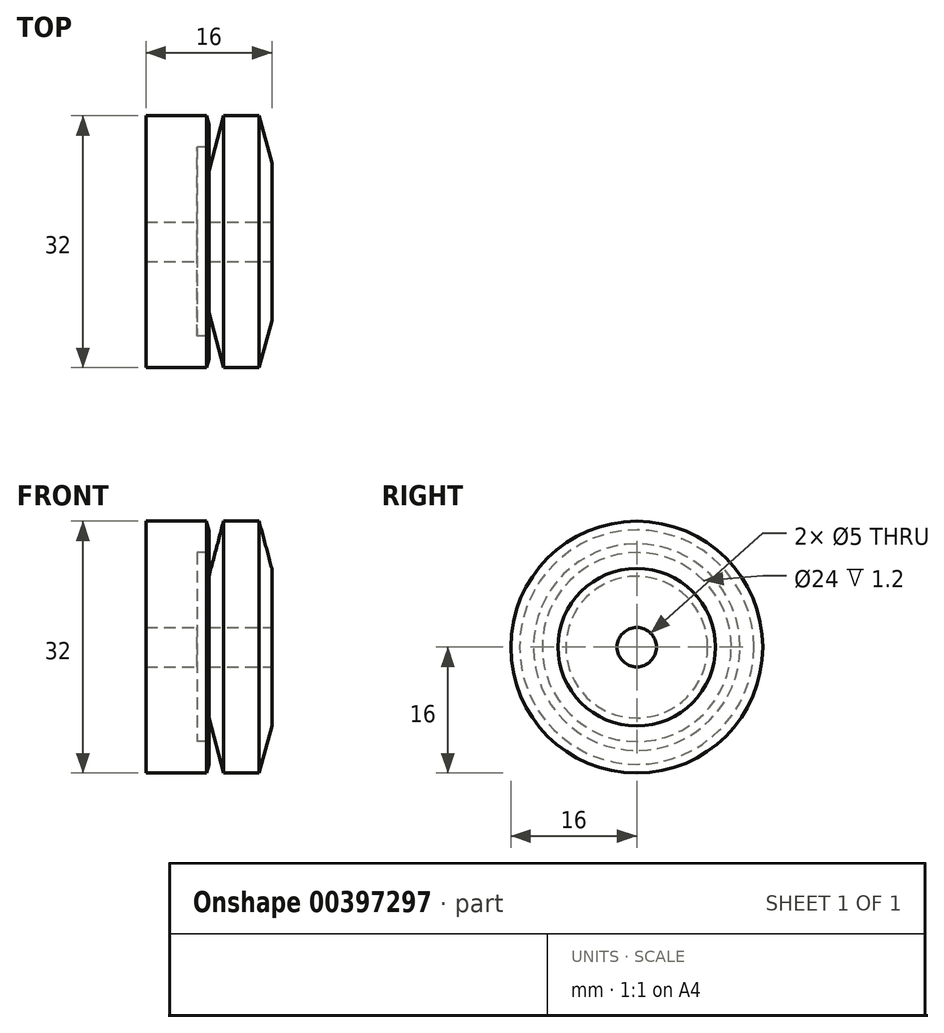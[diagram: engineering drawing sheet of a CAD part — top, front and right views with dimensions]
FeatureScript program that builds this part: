
annotation { "Feature Type Name" : "Feature", "Feature Type Description" : "" }
export const myFeature = defineFeature(function(context is Context, id is Id, definition is map)
    precondition{}
    {
        {
            var Q0;
            Q0=qCreatedBy(makeId("Front.planeOp"),FACE);
            var sketch = newSketch(context, id + "F0", { "sketchPlane" : qUnion([Q0])});
            skLineSegment(sketch, "E0", {"start": v(0, 3) * mm, "end": v(0, 16) * mm});
            skLineSegment(sketch, "E1", {"start": v(0, 16) * mm, "end": v(8, 16) * mm});
            skLineSegment(sketch, "E2", {"start": v(8, 16) * mm, "end": v(8, 12) * mm});
            skLineSegment(sketch, "E3", {"start": v(8, 6) * mm, "end": v(6.5, 6) * mm});
            skLineSegment(sketch, "E4", {"start": v(6.5, 6) * mm, "end": v(6.5, 12) * mm});
            skLineSegment(sketch, "E5", {"start": v(6.5, 12) * mm, "end": v(8, 12) * mm});
            skPoint(sketch, "E6.orphan", {"position": v(0, 0) * mm});
            skLineSegment(sketch, "E7", {"start": v(8, 0) * mm, "end": v(16, 0) * mm});
            skLineSegment(sketch, "E8", {"start": v(16, 0) * mm, "end": v(16, 16) * mm});
            skLineSegment(sketch, "E9", {"start": v(16, 16) * mm, "end": v(9.88, 16) * mm});
            skLineSegment(sketch, "E10", {"start": v(9.88, 16) * mm, "end": v(8, 9) * mm});
            skLineSegment(sketch, "E11", {"start": v(0, 0) * mm, "end": v(0, 16) * mm});
            skLineSegment(sketch, "E12", {"start": v(0, 3) * mm, "end": v(16, 3) * mm, "construction": true});
            skLineSegment(sketch, "E13", {"start": v(0, 0) * mm, "end": v(8, 0) * mm});
            skLineSegment(sketch, "E14", {"start": v(8, 0) * mm, "end": v(8, 6) * mm});
            skLineSegment(sketch, "E15", {"start": v(8.24, 14) * mm, "end": v(7.7, 16) * mm});
            skLineSegment(sketch, "E16", {"start": v(8.24, 14) * mm, "end": v(7.7, 12) * mm});
            skLineSegment(sketch, "E17", {"start": v(8, 9) * mm, "end": v(8, 6) * mm});
            skLineSegment(sketch, "E18", {"start": v(7.7, 16) * mm, "end": v(7.7, 12) * mm, "construction": true});
            skLineSegment(sketch, "E19", {"start": v(6.5, 6) * mm, "end": v(6.5, 0) * mm});
            skLineSegment(sketch, "E20", {"start": v(14.4, 16) * mm, "end": v(16, 10) * mm});
            skSolve(sketch);
        }
        {
            var Q0;
            {var subQ1=sQuery(id+"F0.wireOp",EDGE,"E4");Q0=makeQuery(id+"F0.imprint","IMPRINT",FACE,{"disambiguationData":[TD([[makeQuery(id+"F0.imprint","IMPRINT",EDGE,{"derivedFrom":subQ1}),1.0]])]});}
            var Q1;
            Q1=sQuery(id+"F0.wireOp",EDGE,"E13");
            revolve(context, id + "F1", {"entities" : qUnion([Q0]), "axis" : qUnion([Q1]), "revolveType" : RevolveType.FULL});
        }
        {
            var Q0;
            Q0=makeQuery(id+"F0.imprint","IMPRINT",FACE,{"disambiguationData":[TD([[makeQuery(id+"F0.imprint","IMPRINT",EDGE,{"derivedFrom":sQuery(id+"F0.wireOp",EDGE,"E7")}),1.0]])]});
            var Q1;
            Q1=sQuery(id+"F0.wireOp",EDGE,"E7");
            revolve(context, id + "F2", {"entities" : qUnion([Q0]), "axis" : qUnion([Q1]), "revolveType" : RevolveType.FULL});
        }
        {
            var Q0;
            Q0=makeQuery(id+"F2.opRevolve","SWEPT_FACE",FACE,{"disambiguationData":[OSD([sQuery(id+"F0.wireOp",EDGE,"E8")])]});
            var sketch = newSketch(context, id + "F3", { "sketchPlane" : qUnion([Q0])});
            skPoint(sketch, "E21", {"position": v(0, 0) * mm});
            skSolve(sketch);
        }
        {
            var Q0;
            Q0=sQuery(id+"F3.wireOp",VERTEX,"E21");
            var Q1;
            Q1=makeQuery(id+"F1.opRevolve","SWEPT_BODY",BODY,{"disambiguationData":[OSD([sQuery(id+"F0.wireOp",EDGE,"E1"),sQuery(id+"F0.wireOp",EDGE,"E3"),sQuery(id+"F0.wireOp",EDGE,"E4"),sQuery(id+"F0.wireOp",EDGE,"E5"),sQuery(id+"F0.wireOp",EDGE,"ZnAqVL4D-hQFq-7hlk-x1MC-VtTx1OLwrA9f"),sQuery(id+"F0.wireOp",EDGE,"E11"),sQuery(id+"F0.wireOp",EDGE,"E13"),sQuery(id+"F0.wireOp",EDGE,"E14")])]});
            var Q2;
            Q2=makeQuery(id+"F2.opRevolve","SWEPT_BODY",BODY,{"disambiguationData":[OSD([sQuery(id+"F0.wireOp",EDGE,"E7"),sQuery(id+"F0.wireOp",EDGE,"E8"),sQuery(id+"F0.wireOp",EDGE,"E9"),sQuery(id+"F0.wireOp",EDGE,"E10"),sQuery(id+"F0.wireOp",EDGE,"hAoTT0Az-jcBe-9MR6-X2C5-mULgHwRUkr7G"),sQuery(id+"F0.wireOp",EDGE,"E14")])]});
            hole(context, id + "F4", {"style" : HoleStyle.SIMPLE, "endStyle" : HoleEndStyle.THROUGH, "standardTappedOrClearance" : lookupTablePath({ "standard" : "ISO", "engagement" : "75%", "pitch" : "1 mm", "size" : "M6", "type" : "Tapped" }), "standardBlindInLast" : lookupTablePath({ "standard" : "ISO", "engagement" : "75%", "pitch" : "1 mm", "size" : "M6", "type" : "Tapped" }), "holeDiameter" : 5 * mm, "showTappedDepth" : true, "isTappedThrough" : true, "tappedDepth" : 12 * mm, "tapClearance" : 3, "locations" : qUnion([Q0]), "scope" : qUnion([Q1, Q2]), "majorDiameter" : 6 * mm});
        }
    });
